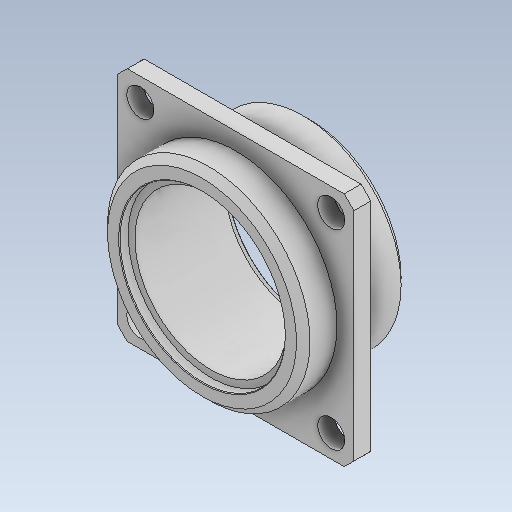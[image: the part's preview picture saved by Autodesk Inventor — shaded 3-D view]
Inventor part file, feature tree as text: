
AUTODESK INVENTOR PART (.ipt)
format: ipt  version: 2023 (Build 270158000, 158)  size: 172,544 bytes
history: native  units: in
note: dims shown in document units (in); Inventor stores cm internally (conversion verified against a paired STEP export)
features: fillet x1
ambient origin geometry x8: Origin, YZ Plane, XZ Plane, XY Plane, X Axis, Y Axis, Z Axis, Center Point
bodies: Solid1 (feature_tree)
feature tree (1):
  fillet  "Fillet2"  [1 undecoded]
note: 1 required parameter value undecoded (feature->parameter linkage not recoverable at this tier; creation-order binding heuristic only, values carry confidence <= 0.55)
